# Revit family: Hager-UNIVERS-Surface_mounted-IP44-With_Cover-With_DIN-NoHosted-CH-it
name_source: partatom
category: Electrical Equipment
units: mm (PartAtom-declared; Revit-internal decimal feet)

## family parameters
Always vertical = Yes
Cut with Voids When Loaded = No
Maintain Annotation Orientation = No
Panel Configuration = Two Columns, Circuits Across
Part Type = Panelboard
Room Calculation Point = No
Round Connector Dimension = Use Diameter
Shared = No
Work Plane-Based = Yes

## types (37) — shared parameters
Code hager = ADD-EC000214_EU
Default Elevation = 1200 mm
EF000007 - colore = bianco
EF000024 - resistente ai raggi UV = No
EF000049 - profondità = 165 mm
EF000116 - numero RAL = 9010
EF001062 - versione EMC = No
EF001088 - possibilità di applicazione = Yes
EF001134 - barra DIN = Yes
EF004462 - tipo di chiusura = altri
EF005474 - grado di protezione (IP) = IP44
EF006244 - coperchio/porta trasparente = No
EF006306 - con serratura = No
EF015941 - porta di trasmissione del segnale = No
ETIM class code = EC000214
ETIM class name = Small distribution board
HG000002-with door or cover-it = Yes
HG000003-Range-it = UNIVERS
HG000005-Thickness-it = 2 mm  [stored 0.00656168 ft]
HG000006-Flush mounted-it = No
HG000011-Empty rows from bottom-it = No
HG000012-Door swing angle-it = 90.00°
HG000013-Door on the left-it = No
HG000014-Door on the right-it = Yes
HG000015-Clearance visibility-it = Yes
HG000016-Door 3D visibility-it = Yes
HG000017-Distance between poles-it = 18 mm  [stored 0.0590551 ft]
HG000060-RAL-number = 9010
HG000099-Onfly Template ID-it-CH = 507532
Manufacturer = Hager
Name BIM&CO = Electricity
Name hager = ADD_Enclosures_EC000214
Reference = Template-Enclosure_EU-EC000214
Uniformat = Low Tension Service & Dist.
Uniformat code = D501001
zero-valued in all types: EF001131 - profondità interna

## per-type parameters (varying)
| type | BC_METADATA | EF000003 - modo di montaggio | EF000008 - larghezza | EF000040 - altezza | EF000118 - con piastra di montaggio | EF000218 - profondità di montaggio | EF000266 - numero di file | EF000332 - altezza di installazione | EF000846 - larghezza di montaggio | EF002950 - numero di unità modulari | EF009212 - tipo di coperchio | EF015776 - morsetto di messa a terra | EF015777 - morsettiera a conduttore neutro | HG000001 - Numero di colonne | HG000004-Manufacturer reference-it | HG000007-Number of empty columns-it | HG000008-Number of empty rows-it | HG000009-Double swing door-it | HG000010-Asymmetric doors-it | HGEF000266-Numero di file | HGEF0002950-larghezza in unità di suddivisione |
| UNIVERS-Surface_mounted_W1050_H1100_D165_48_Modular_Spacing-FWB74S | {"ObjectGuid":"1025db30-4b53-4bc4-8550-e9a74323c3fa","ModelGuid":"d8f3fdfa-0677-4bc0-b703-85c18313e8b9","VariantGuid":"d9b84df5-4ae8-400b-8abf-91724eba98b9","Revision":"#59","VariantName":"UNIVERS-Surface_mounted_W1050_H1100_D165_48_Modular_Spacing-FWB74S"} | apparente/incassato | 1050 mm | 1100 mm  [stored 3.60892 ft] | No | 161 mm  [stored 0.528215 ft] | 7 | 1100 mm  [stored 3.60892 ft] | 1050 mm | 48 | con taglio | Yes | Yes | 4 | FWB74S | 0 | 0 | Yes | No | 7 | 48 |
| UNIVERS-Surface_mounted_W300_H1250_D165_12_Modular_Spacing-FWB81S | {"ObjectGuid":"1025db30-4b53-4bc4-8550-e9a74323c3fa","ModelGuid":"d8f3fdfa-0677-4bc0-b703-85c18313e8b9","VariantGuid":"9c9d503c-c3c6-49fe-b68e-4a099a8b2c35","Revision":"#59","VariantName":"UNIVERS-Surface_mounted_W300_H1250_D165_12_Modular_Spacing-FWB81S"} | apparente | 300 mm | 1250 mm  [stored 4.10105 ft] | No | 161 mm  [stored 0.528215 ft] | 8 | 1250 mm  [stored 4.10105 ft] | 300 mm | 12 | chiuso | Yes | Yes | 1 | FWB81S | 0 | 0 | No | No | 8 | 12 |
| UNIVERS-Surface_mounted_W300_H500_D165_12_Modular_Spacing-FWB31S | {"ObjectGuid":"1025db30-4b53-4bc4-8550-e9a74323c3fa","ModelGuid":"d8f3fdfa-0677-4bc0-b703-85c18313e8b9","VariantGuid":"bb68b575-c385-4183-8824-e39ed3a1ace8","Revision":"#59","VariantName":"UNIVERS-Surface_mounted_W300_H500_D165_12_Modular_Spacing-FWB31S"} | apparente | 300 mm | 500 mm  [stored 1.64042 ft] | No | 161 mm  [stored 0.528215 ft] | 3 | 500 mm  [stored 1.64042 ft] | 300 mm | 12 | con taglio | Yes | Yes | 1 | FWB31S | 0 | 0 | No | No | 3 | 12 |
| UNIVERS-Surface_mounted_W550_H500_D165_24_Modular_Spacing-FWB32S | {"ObjectGuid":"1025db30-4b53-4bc4-8550-e9a74323c3fa","ModelGuid":"d8f3fdfa-0677-4bc0-b703-85c18313e8b9","VariantGuid":"051328bd-ef11-4318-a192-e2e229fc472d","Revision":"#59","VariantName":"UNIVERS-Surface_mounted_W550_H500_D165_24_Modular_Spacing-FWB32S"} | apparente | 550 mm | 500 mm  [stored 1.64042 ft] | No | 161 mm  [stored 0.528215 ft] | 3 | 500 mm  [stored 1.64042 ft] | 550 mm | 24 | con taglio | Yes | Yes | 2 | FWB32S | 0 | 0 | No | No | 3 | 24 |
| UNIVERS-Surface_mounted_W800_H500_D165_36_Modular_Spacing-FWB33S | {"ObjectGuid":"1025db30-4b53-4bc4-8550-e9a74323c3fa","ModelGuid":"d8f3fdfa-0677-4bc0-b703-85c18313e8b9","VariantGuid":"d40fb7fe-30bf-47e6-afcd-41040368116e","Revision":"#59","VariantName":"UNIVERS-Surface_mounted_W800_H500_D165_36_Modular_Spacing-FWB33S"} | apparente | 800 mm  [stored 2.62467 ft] | 500 mm  [stored 1.64042 ft] | No | 161 mm  [stored 0.528215 ft] | 3 | 500 mm  [stored 1.64042 ft] | 800 mm  [stored 2.62467 ft] | 36 | con taglio | Yes | Yes | 3 | FWB33S | 0 | 0 | Yes | Yes | 3 | 36 |
| UNIVERS-Surface_mounted_W1050_H500_D165_48_Modular_Spacing-FWB34S | {"ObjectGuid":"1025db30-4b53-4bc4-8550-e9a74323c3fa","ModelGuid":"d8f3fdfa-0677-4bc0-b703-85c18313e8b9","VariantGuid":"69664598-4ca1-4792-89af-4f4ac7567254","Revision":"#59","VariantName":"UNIVERS-Surface_mounted_W1050_H500_D165_48_Modular_Spacing-FWB34S"} | apparente | 1050 mm | 500 mm  [stored 1.64042 ft] | No | 161 mm  [stored 0.528215 ft] | 3 | 500 mm  [stored 1.64042 ft] | 1050 mm | 48 | con taglio | Yes | Yes | 4 | FWB34S | 0 | 0 | Yes | No | 3 | 48 |
| UNIVERS-Surface_mounted_W300_H650_D165_12_Modular_Spacing-FWB41S | {"ObjectGuid":"1025db30-4b53-4bc4-8550-e9a74323c3fa","ModelGuid":"d8f3fdfa-0677-4bc0-b703-85c18313e8b9","VariantGuid":"eaeb4b58-28da-4b96-a45f-98399f194030","Revision":"#59","VariantName":"UNIVERS-Surface_mounted_W300_H650_D165_12_Modular_Spacing-FWB41S"} | apparente | 300 mm | 650 mm  [stored 2.13255 ft] | No | 161 mm  [stored 0.528215 ft] | 4 | 650 mm  [stored 2.13255 ft] | 300 mm | 12 | con taglio | Yes | Yes | 1 | FWB41S | 0 | 0 | No | No | 4 | 12 |
| UNIVERS-Surface_mounted_W550_H650_D165_24_Modular_Spacing-FWB42K5 | {"ObjectGuid":"1025db30-4b53-4bc4-8550-e9a74323c3fa","ModelGuid":"d8f3fdfa-0677-4bc0-b703-85c18313e8b9","VariantGuid":"76b41440-608e-48a6-aed3-06b0488f5fe4","Revision":"#59","VariantName":"UNIVERS-Surface_mounted_W550_H650_D165_24_Modular_Spacing-FWB42K5"} | apparente | 550 mm | 650 mm  [stored 2.13255 ft] | Yes | 161 mm  [stored 0.528215 ft] | 4 | 650 mm  [stored 2.13255 ft] | 550 mm | 24 | con taglio | Yes | No | 2 | FWB42K5 | 1 | 0 | No | No | 4 | 24 |
| UNIVERS-Surface_mounted_W550_H650_D165_24_Modular_Spacing-FWB42P2 | {"ObjectGuid":"1025db30-4b53-4bc4-8550-e9a74323c3fa","ModelGuid":"d8f3fdfa-0677-4bc0-b703-85c18313e8b9","VariantGuid":"a1431b4b-fef4-416a-aeee-88220733db78","Revision":"#59","VariantName":"UNIVERS-Surface_mounted_W550_H650_D165_24_Modular_Spacing-FWB42P2"} | apparente/incassato | 550 mm | 650 mm  [stored 2.13255 ft] | No | 161 mm  [stored 0.528215 ft] | 4 | 650 mm  [stored 2.13255 ft] | 550 mm | 24 | con taglio | Yes | No | 1 | FWB42P2 | 1 | 0 | No | No | 4 | 24 |
| UNIVERS-Surface_mounted_W550_H650_D165_24_Modular_Spacing-FWB42S | {"ObjectGuid":"1025db30-4b53-4bc4-8550-e9a74323c3fa","ModelGuid":"d8f3fdfa-0677-4bc0-b703-85c18313e8b9","VariantGuid":"ac68dd3f-efee-48b4-b5d0-3297dfa41004","Revision":"#59","VariantName":"UNIVERS-Surface_mounted_W550_H650_D165_24_Modular_Spacing-FWB42S"} | apparente/incassato | 550 mm | 650 mm  [stored 2.13255 ft] | No | 161 mm  [stored 0.528215 ft] | 4 | 650 mm  [stored 2.13255 ft] | 550 mm | 24 | con taglio | Yes | Yes | 2 | FWB42S | 0 | 0 | No | No | 4 | 24 |
| UNIVERS-Surface_mounted_W800_H650_D165_36_Modular_Spacing-FWB43S | {"ObjectGuid":"1025db30-4b53-4bc4-8550-e9a74323c3fa","ModelGuid":"d8f3fdfa-0677-4bc0-b703-85c18313e8b9","VariantGuid":"c1610af8-22a2-44ec-a3d5-724fc58b37aa","Revision":"#59","VariantName":"UNIVERS-Surface_mounted_W800_H650_D165_36_Modular_Spacing-FWB43S"} | apparente | 800 mm  [stored 2.62467 ft] | 650 mm  [stored 2.13255 ft] | No | 161 mm  [stored 0.528215 ft] | 4 | 650 mm  [stored 2.13255 ft] | 800 mm  [stored 2.62467 ft] | 36 | con taglio | Yes | Yes | 3 | FWB43S | 0 | 0 | Yes | Yes | 4 | 36 |
| UNIVERS-Surface_mounted_W1050_H650_D165_48_Modular_Spacing-FWB44S | {"ObjectGuid":"1025db30-4b53-4bc4-8550-e9a74323c3fa","ModelGuid":"d8f3fdfa-0677-4bc0-b703-85c18313e8b9","VariantGuid":"67bfe4ba-aae0-41a8-8daf-a571e6b7a161","Revision":"#59","VariantName":"UNIVERS-Surface_mounted_W1050_H650_D165_48_Modular_Spacing-FWB44S"} | apparente | 1050 mm | 650 mm  [stored 2.13255 ft] | No | 161 mm  [stored 0.528215 ft] | 4 | 650 mm  [stored 2.13255 ft] | 1050 mm | 48 | con taglio | Yes | Yes | 4 | FWB44S | 0 | 0 | Yes | No | 4 | 48 |
| UNIVERS-Surface_mounted_W300_H800_D165_12_Modular_Spacing-FWB51S | {"ObjectGuid":"1025db30-4b53-4bc4-8550-e9a74323c3fa","ModelGuid":"d8f3fdfa-0677-4bc0-b703-85c18313e8b9","VariantGuid":"770b0aef-4d3e-4ba9-960e-a3a9e7ee2106","Revision":"#59","VariantName":"UNIVERS-Surface_mounted_W300_H800_D165_12_Modular_Spacing-FWB51S"} | apparente | 300 mm | 800 mm  [stored 2.62467 ft] | No | 161 mm  [stored 0.528215 ft] | 5 | 800 mm  [stored 2.62467 ft] | 300 mm | 12 | con taglio | Yes | Yes | 1 | FWB51S | 0 | 0 | No | No | 5 | 12 |
| UNIVERS-Surface_mounted_W550_H800_D165_24_Modular_Spacing-FWB52K5 | {"ObjectGuid":"1025db30-4b53-4bc4-8550-e9a74323c3fa","ModelGuid":"d8f3fdfa-0677-4bc0-b703-85c18313e8b9","VariantGuid":"315dd730-be28-4be7-b24e-8f0a14252a90","Revision":"#59","VariantName":"UNIVERS-Surface_mounted_W550_H800_D165_24_Modular_Spacing-FWB52K5"} | apparente | 550 mm | 800 mm  [stored 2.62467 ft] | Yes | 161 mm  [stored 0.528215 ft] | 5 | 800 mm  [stored 2.62467 ft] | 550 mm | 24 | con taglio | Yes | No | 2 | FWB52K5 | 1 | 0 | No | No | 5 | 24 |
| UNIVERS-Surface_mounted_W550_H800_D165_24_Modular_Spacing-FWB52N3 | {"ObjectGuid":"1025db30-4b53-4bc4-8550-e9a74323c3fa","ModelGuid":"d8f3fdfa-0677-4bc0-b703-85c18313e8b9","VariantGuid":"4c8b2cc6-46d8-4da4-adea-d86653345a76","Revision":"#59","VariantName":"UNIVERS-Surface_mounted_W550_H800_D165_24_Modular_Spacing-FWB52N3"} | apparente | 550 mm | 800 mm  [stored 2.62467 ft] | No | 160 mm  [stored 0.524934 ft] | 5 | 800 mm  [stored 2.62467 ft] | 550 mm | 24 | con taglio | No | No | 2 | FWB52N3 | 0 | 2 | No | No | 5 | 24 |
| UNIVERS-Surface_mounted_W550_H800_D165_24_Modular_Spacing-FWB52P2 | {"ObjectGuid":"1025db30-4b53-4bc4-8550-e9a74323c3fa","ModelGuid":"d8f3fdfa-0677-4bc0-b703-85c18313e8b9","VariantGuid":"6262887b-680c-43b0-9149-78f8e2228664","Revision":"#59","VariantName":"UNIVERS-Surface_mounted_W550_H800_D165_24_Modular_Spacing-FWB52P2"} | apparente/incassato | 550 mm | 800 mm  [stored 2.62467 ft] | No | 161 mm  [stored 0.528215 ft] | 5 | 800 mm  [stored 2.62467 ft] | 550 mm | 24 | con taglio | Yes | No | 1 | FWB52P2 | 1 | 0 | No | No | 5 | 24 |
| UNIVERS-Surface_mounted_W550_H800_D165_24_Modular_Spacing-FWB52S | {"ObjectGuid":"1025db30-4b53-4bc4-8550-e9a74323c3fa","ModelGuid":"d8f3fdfa-0677-4bc0-b703-85c18313e8b9","VariantGuid":"a0197769-1a5b-4c6c-9ed9-81d6c987d11d","Revision":"#59","VariantName":"UNIVERS-Surface_mounted_W550_H800_D165_24_Modular_Spacing-FWB52S"} | apparente | 550 mm | 800 mm  [stored 2.62467 ft] | No | 161 mm  [stored 0.528215 ft] | 5 | 800 mm  [stored 2.62467 ft] | 550 mm | 24 | con taglio | Yes | Yes | 2 | FWB52S | 0 | 0 | No | No | 5 | 24 |
| UNIVERS-Surface_mounted_W800_H800_D165_36_Modular_Spacing-FWB53K5 | {"ObjectGuid":"1025db30-4b53-4bc4-8550-e9a74323c3fa","ModelGuid":"d8f3fdfa-0677-4bc0-b703-85c18313e8b9","VariantGuid":"c48df4a8-2b4d-47d1-9e22-2054415158ed","Revision":"#59","VariantName":"UNIVERS-Surface_mounted_W800_H800_D165_36_Modular_Spacing-FWB53K5"} | apparente | 800 mm  [stored 2.62467 ft] | 800 mm  [stored 2.62467 ft] | Yes | 161 mm  [stored 0.528215 ft] | 5 | 800 mm  [stored 2.62467 ft] | 800 mm  [stored 2.62467 ft] | 36 | con taglio | Yes | No | 2 | FWB53K5 | 1 | 0 | Yes | Yes | 5 | 36 |
| UNIVERS-Surface_mounted_W800_H800_D165_36_Modular_Spacing-FWB53N3 | {"ObjectGuid":"1025db30-4b53-4bc4-8550-e9a74323c3fa","ModelGuid":"d8f3fdfa-0677-4bc0-b703-85c18313e8b9","VariantGuid":"698d3efa-6174-40ca-a66c-541cba8e72e2","Revision":"#59","VariantName":"UNIVERS-Surface_mounted_W800_H800_D165_36_Modular_Spacing-FWB53N3"} | apparente | 800 mm  [stored 2.62467 ft] | 800 mm  [stored 2.62467 ft] | No | 161 mm  [stored 0.528215 ft] | 5 | 800 mm  [stored 2.62467 ft] | 800 mm  [stored 2.62467 ft] | 36 | con taglio | No | No | 3 | FWB53N3 | 0 | 2 | Yes | Yes | 5 | 36 |
| UNIVERS-Surface_mounted_W800_H800_D165_36_Modular_Spacing-FWB53S | {"ObjectGuid":"1025db30-4b53-4bc4-8550-e9a74323c3fa","ModelGuid":"d8f3fdfa-0677-4bc0-b703-85c18313e8b9","VariantGuid":"cbc582e0-4d0a-423c-a1c4-364a2300ee47","Revision":"#59","VariantName":"UNIVERS-Surface_mounted_W800_H800_D165_36_Modular_Spacing-FWB53S"} | apparente | 800 mm  [stored 2.62467 ft] | 800 mm  [stored 2.62467 ft] | No | 161 mm  [stored 0.528215 ft] | 5 | 800 mm  [stored 2.62467 ft] | 800 mm  [stored 2.62467 ft] | 36 | con taglio | Yes | Yes | 3 | FWB53S | 0 | 0 | Yes | Yes | 5 | 36 |
| UNIVERS-Surface_mounted_W1050_H800_D165_48_Modular_Spacing-FWB54S | {"ObjectGuid":"1025db30-4b53-4bc4-8550-e9a74323c3fa","ModelGuid":"d8f3fdfa-0677-4bc0-b703-85c18313e8b9","VariantGuid":"caafa364-bcd3-49d6-9369-9ce7dc670bd7","Revision":"#59","VariantName":"UNIVERS-Surface_mounted_W1050_H800_D165_48_Modular_Spacing-FWB54S"} | apparente | 1050 mm | 800 mm  [stored 2.62467 ft] | No | 161 mm  [stored 0.528215 ft] | 5 | 800 mm  [stored 2.62467 ft] | 1050 mm | 48 | con taglio | Yes | Yes | 4 | FWB54S | 0 | 0 | Yes | No | 5 | 48 |
| UNIVERS-Surface_mounted_W300_H950_D165_12_Modular_Spacing-FWB61S | {"ObjectGuid":"1025db30-4b53-4bc4-8550-e9a74323c3fa","ModelGuid":"d8f3fdfa-0677-4bc0-b703-85c18313e8b9","VariantGuid":"acce0272-460c-4043-8592-7ee0197cd771","Revision":"#59","VariantName":"UNIVERS-Surface_mounted_W300_H950_D165_12_Modular_Spacing-FWB61S"} | apparente | 300 mm | 950 mm  [stored 3.1168 ft] | No | 161 mm  [stored 0.528215 ft] | 6 | 950 mm  [stored 3.1168 ft] | 300 mm | 12 | con taglio | Yes | Yes | 1 | FWB61S | 0 | 0 | No | No | 6 | 12 |
| UNIVERS-Surface_mounted_W550_H950_D165_24_Modular_Spacing-FWB62K5 | {"ObjectGuid":"1025db30-4b53-4bc4-8550-e9a74323c3fa","ModelGuid":"d8f3fdfa-0677-4bc0-b703-85c18313e8b9","VariantGuid":"1f86ea72-5995-4e3d-a5ef-67c129bcd8db","Revision":"#59","VariantName":"UNIVERS-Surface_mounted_W550_H950_D165_24_Modular_Spacing-FWB62K5"} | apparente | 550 mm | 950 mm  [stored 3.1168 ft] | Yes | 161 mm  [stored 0.528215 ft] | 6 | 950 mm  [stored 3.1168 ft] | 550 mm | 24 | con taglio | Yes | No | 1 | FWB62K5 | 1 | 0 | No | No | 6 | 24 |
| UNIVERS-Surface_mounted_W550_H950_D165_24_Modular_Spacing-FWB62N3 | {"ObjectGuid":"1025db30-4b53-4bc4-8550-e9a74323c3fa","ModelGuid":"d8f3fdfa-0677-4bc0-b703-85c18313e8b9","VariantGuid":"1cbe2c17-e23b-44c7-9f8b-05ffa1fa7abc","Revision":"#59","VariantName":"UNIVERS-Surface_mounted_W550_H950_D165_24_Modular_Spacing-FWB62N3"} | apparente | 550 mm | 950 mm  [stored 3.1168 ft] | No | 161 mm  [stored 0.528215 ft] | 6 | 950 mm  [stored 3.1168 ft] | 550 mm | 24 | con taglio | No | No | 2 | FWB62N3 | 0 | 2 | No | No | 6 | 24 |
| UNIVERS-Surface_mounted_W550_H950_D165_24_Modular_Spacing-FWB62S | {"ObjectGuid":"1025db30-4b53-4bc4-8550-e9a74323c3fa","ModelGuid":"d8f3fdfa-0677-4bc0-b703-85c18313e8b9","VariantGuid":"8d4aaf76-4fa4-407d-adb9-1b43ddf5043b","Revision":"#59","VariantName":"UNIVERS-Surface_mounted_W550_H950_D165_24_Modular_Spacing-FWB62S"} | apparente | 550 mm | 950 mm  [stored 3.1168 ft] | No | 161 mm  [stored 0.528215 ft] | 6 | 950 mm  [stored 3.1168 ft] | 550 mm | 24 | con taglio | Yes | Yes | 2 | FWB62S | 0 | 0 | No | No | 6 | 24 |
| UNIVERS-Surface_mounted_W800_H950_D165_36_Modular_Spacing-FWB63K5 | {"ObjectGuid":"1025db30-4b53-4bc4-8550-e9a74323c3fa","ModelGuid":"d8f3fdfa-0677-4bc0-b703-85c18313e8b9","VariantGuid":"3dd86c58-737c-49af-8ac7-011d0b2ab9b9","Revision":"#59","VariantName":"UNIVERS-Surface_mounted_W800_H950_D165_36_Modular_Spacing-FWB63K5"} | apparente | 800 mm  [stored 2.62467 ft] | 950 mm  [stored 3.1168 ft] | Yes | 161 mm  [stored 0.528215 ft] | 6 | 950 mm  [stored 3.1168 ft] | 800 mm  [stored 2.62467 ft] | 36 | con taglio | Yes | No | 2 | FWB63K5 | 1 | 0 | Yes | Yes | 6 | 36 |
| UNIVERS-Surface_mounted_W800_H950_D165_36_Modular_Spacing-FWB63N3 | {"ObjectGuid":"1025db30-4b53-4bc4-8550-e9a74323c3fa","ModelGuid":"d8f3fdfa-0677-4bc0-b703-85c18313e8b9","VariantGuid":"ca80cda4-c97e-4158-bd78-70d0fded7555","Revision":"#59","VariantName":"UNIVERS-Surface_mounted_W800_H950_D165_36_Modular_Spacing-FWB63N3"} | apparente | 800 mm  [stored 2.62467 ft] | 950 mm  [stored 3.1168 ft] | No | 161 mm  [stored 0.528215 ft] | 6 | 950 mm  [stored 3.1168 ft] | 800 mm  [stored 2.62467 ft] | 36 | con taglio | No | No | 3 | FWB63N3 | 0 | 2 | Yes | Yes | 6 | 36 |
| UNIVERS-Surface_mounted_W800_H950_D165_36_Modular_Spacing-FWB63S | {"ObjectGuid":"1025db30-4b53-4bc4-8550-e9a74323c3fa","ModelGuid":"d8f3fdfa-0677-4bc0-b703-85c18313e8b9","VariantGuid":"abe9cd14-7334-43d6-9776-6da262f33cea","Revision":"#59","VariantName":"UNIVERS-Surface_mounted_W800_H950_D165_36_Modular_Spacing-FWB63S"} | apparente | 800 mm  [stored 2.62467 ft] | 950 mm  [stored 3.1168 ft] | No | 161 mm  [stored 0.528215 ft] | 6 | 950 mm  [stored 3.1168 ft] | 800 mm  [stored 2.62467 ft] | 36 | con taglio | Yes | Yes | 3 | FWB63S | 0 | 0 | Yes | Yes | 6 | 36 |
| UNIVERS-Surface_mounted_W1050_H950_D165_48_Modular_Spacing-FWB64N3 | {"ObjectGuid":"1025db30-4b53-4bc4-8550-e9a74323c3fa","ModelGuid":"d8f3fdfa-0677-4bc0-b703-85c18313e8b9","VariantGuid":"5bfa5d60-e66b-4466-8dc6-e4914aa7b163","Revision":"#59","VariantName":"UNIVERS-Surface_mounted_W1050_H950_D165_48_Modular_Spacing-FWB64N3"} | apparente | 1050 mm | 950 mm  [stored 3.1168 ft] | No | 161 mm  [stored 0.528215 ft] | 6 | 950 mm  [stored 3.1168 ft] | 1050 mm | 48 | con taglio | No | No | 4 | FWB64N3 | 0 | 2 | Yes | No | 6 | 48 |
| UNIVERS-Surface_mounted_W1050_H950_D165_48_Modular_Spacing-FWB64S | {"ObjectGuid":"1025db30-4b53-4bc4-8550-e9a74323c3fa","ModelGuid":"d8f3fdfa-0677-4bc0-b703-85c18313e8b9","VariantGuid":"001a657f-3210-43f4-8f27-42f7ecb6a104","Revision":"#59","VariantName":"UNIVERS-Surface_mounted_W1050_H950_D165_48_Modular_Spacing-FWB64S"} | apparente | 1050 mm | 950 mm  [stored 3.1168 ft] | No | 161 mm  [stored 0.528215 ft] | 6 | 950 mm  [stored 3.1168 ft] | 1050 mm | 48 | con taglio | Yes | Yes | 4 | FWB64S | 0 | 0 | Yes | No | 6 | 48 |
| UNIVERS-Surface_mounted_W300_H1100_D165_12_Modular_Spacing-FWB71S | {"ObjectGuid":"1025db30-4b53-4bc4-8550-e9a74323c3fa","ModelGuid":"d8f3fdfa-0677-4bc0-b703-85c18313e8b9","VariantGuid":"17a9cb1d-e1e7-479d-a4c7-77ea07aa208e","Revision":"#59","VariantName":"UNIVERS-Surface_mounted_W300_H1100_D165_12_Modular_Spacing-FWB71S"} | apparente | 300 mm | 1100 mm  [stored 3.60892 ft] | No | 161 mm  [stored 0.528215 ft] | 7 | 1100 mm  [stored 3.60892 ft] | 300 mm | 12 | con taglio | Yes | Yes | 1 | FWB71S | 0 | 0 | No | No | 7 | 12 |
| UNIVERS-Surface_mounted_W550_H1100_D165_24_Modular_Spacing-FWB72K5 | {"ObjectGuid":"1025db30-4b53-4bc4-8550-e9a74323c3fa","ModelGuid":"d8f3fdfa-0677-4bc0-b703-85c18313e8b9","VariantGuid":"8c775c91-5d5d-4349-8df5-82aa81e62ebe","Revision":"#59","VariantName":"UNIVERS-Surface_mounted_W550_H1100_D165_24_Modular_Spacing-FWB72K5"} | apparente | 550 mm | 1100 mm  [stored 3.60892 ft] | Yes | 161 mm  [stored 0.528215 ft] | 7 | 1100 mm  [stored 3.60892 ft] | 550 mm | 24 | con taglio | Yes | No | 1 | FWB72K5 | 1 | 0 | No | No | 7 | 24 |
| UNIVERS-Surface_mounted_W550_H1100_D165_24_Modular_Spacing-FWB72N3 | {"ObjectGuid":"1025db30-4b53-4bc4-8550-e9a74323c3fa","ModelGuid":"d8f3fdfa-0677-4bc0-b703-85c18313e8b9","VariantGuid":"6d63cf1e-c29c-4e08-b522-d7ee9a470d48","Revision":"#59","VariantName":"UNIVERS-Surface_mounted_W550_H1100_D165_24_Modular_Spacing-FWB72N3"} | apparente | 550 mm | 1100 mm  [stored 3.60892 ft] | No | 161 mm  [stored 0.528215 ft] | 7 | 1100 mm  [stored 3.60892 ft] | 550 mm | 24 | con taglio | No | No | 2 | FWB72N3 | 0 | 2 | No | No | 7 | 24 |
| UNIVERS-Surface_mounted_W550_H1100_D165_24_Modular_Spacing-FWB72S | {"ObjectGuid":"1025db30-4b53-4bc4-8550-e9a74323c3fa","ModelGuid":"d8f3fdfa-0677-4bc0-b703-85c18313e8b9","VariantGuid":"af2f57f2-2f8e-4441-adfd-62b60c18c3b1","Revision":"#59","VariantName":"UNIVERS-Surface_mounted_W550_H1100_D165_24_Modular_Spacing-FWB72S"} | apparente/incassato | 550 mm | 1100 mm  [stored 3.60892 ft] | No | 161 mm  [stored 0.528215 ft] | 7 | 1100 mm  [stored 3.60892 ft] | 550 mm | 24 | con taglio | Yes | Yes | 2 | FWB72S | 0 | 0 | No | No | 7 | 24 |
| UNIVERS-Surface_mounted_W800_H1100_D165_36_Modular_Spacing-FWB73N3 | {"ObjectGuid":"1025db30-4b53-4bc4-8550-e9a74323c3fa","ModelGuid":"d8f3fdfa-0677-4bc0-b703-85c18313e8b9","VariantGuid":"0f094a90-5a7f-4fff-85a2-a054d086d0e6","Revision":"#59","VariantName":"UNIVERS-Surface_mounted_W800_H1100_D165_36_Modular_Spacing-FWB73N3"} | apparente | 800 mm  [stored 2.62467 ft] | 1100 mm  [stored 3.60892 ft] | No | 161 mm  [stored 0.528215 ft] | 7 | 1100 mm  [stored 3.60892 ft] | 800 mm  [stored 2.62467 ft] | 36 | con taglio | No | No | 3 | FWB73N3 | 0 | 2 | Yes | Yes | 7 | 36 |
| UNIVERS-Surface_mounted_W800_H1100_D165_36_Modular_Spacing-FWB73S | {"ObjectGuid":"1025db30-4b53-4bc4-8550-e9a74323c3fa","ModelGuid":"d8f3fdfa-0677-4bc0-b703-85c18313e8b9","VariantGuid":"5a063fac-f181-4210-91a3-db553b5be640","Revision":"#59","VariantName":"UNIVERS-Surface_mounted_W800_H1100_D165_36_Modular_Spacing-FWB73S"} | apparente/incassato | 800 mm  [stored 2.62467 ft] | 1100 mm  [stored 3.60892 ft] | No | 161 mm  [stored 0.528215 ft] | 7 | 1100 mm  [stored 3.60892 ft] | 800 mm  [stored 2.62467 ft] | 36 | con taglio | Yes | Yes | 3 | FWB73S | 0 | 0 | Yes | Yes | 7 | 36 |
| UNIVERS-Surface_mounted_W1050_H1100_D165_48_Modular_Spacing-FWB74N3 | {"ObjectGuid":"1025db30-4b53-4bc4-8550-e9a74323c3fa","ModelGuid":"d8f3fdfa-0677-4bc0-b703-85c18313e8b9","VariantGuid":"517b9be8-762c-4d9f-8b03-fa588bc5d3ef","Revision":"#59","VariantName":"UNIVERS-Surface_mounted_W1050_H1100_D165_48_Modular_Spacing-FWB74N3"} | apparente | 1050 mm | 1100 mm  [stored 3.60892 ft] | No | 161 mm  [stored 0.528215 ft] | 7 | 1100 mm  [stored 3.60892 ft] | 1050 mm | 48 | con taglio | No | No | 4 | FWB74N3 | 0 | 2 | Yes | No | 7 | 48 |

note: [stored X ft] marks values corroborated as IEEE doubles in the binary element streams (Revit-internal decimal feet)

## geometry (parser evidence)
native form markers: Sweep x14
no freeform markers — native parametric forms only
